# Revit family: Hager-Univers-IP54-D205-H1100-Cl.II-Encl-NoHosted-PL-pl
name_source: partatom
category: Electrical Equipment
units: mm (PartAtom-declared; Revit-internal decimal feet)

## family parameters
Always vertical = Yes
Cut with Voids When Loaded = No
Panel Configuration = Two Columns, Circuits Across
Part Type = Panelboard
Room Calculation Point = No
Round Connector Dimension = Use Diameter
Shared = No
Work Plane-Based = Yes

## types (5) — shared parameters
Default Elevation = 1219 mm
EF000003 - Sposób montażu = EV000384 - Montaż natynkowy
EF000007 - Kolor = EV000202 - Biały
EF000040 - Wysokość = 1100 mm
EF000049 - Głębokość = 205 mm  [stored 0.672572 ft]
EF000116 - Numer RAL = 9010
EF000118 - Z płytą montażową = No
EF000218 - Głębokość wbudowania = 205 mm  [stored 0.672572 ft]
EF000266 - Liczba rzędów = 7
EF000339 - Rodzaj pokrywy = EV004216 - Drzwi
EF001088 - Możliwość rozbudowy = Yes
EF001131 - Głębokość wewnętrzna = 130 mm  [stored 0.426509 ft]
EF001596 - Materiał obudowy = EV000179 - Stal
EF001613 - Podtrzymanie funkcji = EV000494 - Brak
EF003532 - Do zastosowań zewnętrznych = No
EF004293 - Odporność udarowa = EV006815 - IK09
EF005474 - Stopień ochrony (IP) = EV006419 - IP54
EF006244 - Transparentna pokrywa/drzwi = No
EF006306 - Z zamkiem = No
EF007800 - Do ochrony odgromowej = No
EF008873 - Prąd znamionowy (In) = 250 A
EF009170 - Obudowa z materiału o wysokiej wytrzymałości mechanicznej = 1 mm  [stored 0.00328084 ft]
EF009171 - Drzwi/pokrywa z materiału o wysokiej wytrzymałości mechanicznej = 1 mm  [stored 0.00328084 ft]
EF009212 - Wykonanie pokrywy = EV000116 - Zamknięty
EF015940 - Pokrywa z wyzwalaczem nadciśnieniowym = No
HG000002 - Z drzwiami lub pokrywą = Yes
HG000003 - Zakres = Univers
HG000006 - Montaż podtynkowy = No
HG000023 - Obudowa dwusekcyjna = No
HG000024 - Wysokość części dolnej = 600 mm
HG000026 - Stojąca = No
Manufacturer = Hager
Type Comments = Univers
zero-valued in all types: HG000027 - Wysokość cokołu

## per-type parameters (varying)
| type | EF000008 - Szerokość | EF000437 - Liczba wejść kablowych | EF002950 - Szerokość wyrażona liczbą modułów | EF004427 - Liczba modułów | EF004464 - Rodzaj drzwi | EF009554 - Liczba otworów pod flansze | HG000004 - Referencja producenta | HG000009 - Drzwi dwuskrzydłowe | HG000010 - Drzwi asymetryczne |
| Montaż natynkowy IP54 S1050 W1100 G205  - FP74SW2 | 1050 mm | 8 | 48 | 336 | EV003602 - Podwójny | 8 | FP74SW2 | Yes | No |
| Montaż natynkowy IP54 S1300 W1100 G205  - FP75SW2 | 1300 mm  [stored 4.26509 ft] | 10 | 60 | 420 | EV003602 - Podwójny | 10 | FP75SW2 | Yes | Yes |
| Montaż natynkowy IP54 S300 W1100 G205  - FP71SW2 | 300 mm | 2 | 12 | 84 | EV002646 - Pojedynczy | 2 | FP71SW2 | No | No |
| Montaż natynkowy IP54 S550 W1100 G205  - FP72SW2 | 550 mm | 4 | 24 | 168 | EV002646 - Pojedynczy | 4 | FP72SW2 | No | No |
| Montaż natynkowy IP54 S800 W1100 G205  - FP73SW2 | 800 mm  [stored 2.62467 ft] | 6 | 36 | 252 | EV002646 - Pojedynczy | 6 | FP73SW2 | No | No |

note: [stored X ft] marks values corroborated as IEEE doubles in the binary element streams (Revit-internal decimal feet)

## geometry (parser evidence)
native form markers: Blend x4, Sweep x11
no freeform markers — native parametric forms only
